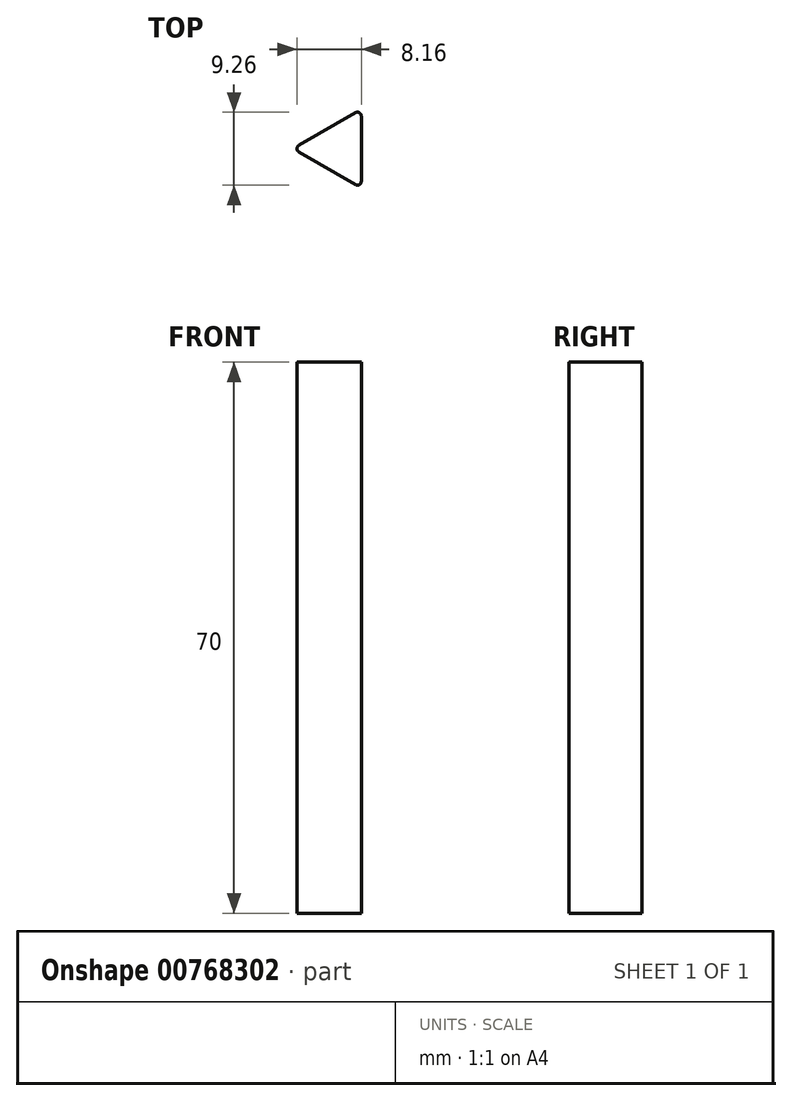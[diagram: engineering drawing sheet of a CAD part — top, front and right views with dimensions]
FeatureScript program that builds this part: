
annotation { "Feature Type Name" : "Feature", "Feature Type Description" : "" }
export const myFeature = defineFeature(function(context is Context, id is Id, definition is map)
    precondition{}
    {
        {
            var Q0;
            Q0=qCreatedBy(makeId("Top.planeOp"),FACE);
            var sketch = newSketch(context, id + "F0", { "sketchPlane" : qUnion([Q0])});
            skCircle(sketch, "E0.cCircle", {"center": v(0, 0) * mm, "radius": 5.77 * mm, "construction": true});
            skLineSegment(sketch, "E0.0", {"start": v(-5.02, 0.43) * mm, "end": v(2.14, 4.57) * mm});
            skLineSegment(sketch, "E0.1", {"start": v(2.89, 4.13) * mm, "end": v(2.89, -4.13) * mm});
            skLineSegment(sketch, "E0.2", {"start": v(2.14, -4.57) * mm, "end": v(-5.02, -0.43) * mm});
            skPoint(sketch, "E1.visualSharp", {"position": v(2.89, 5) * mm});
            skArc(sketch, "E1.filletArc", {"start": v(2.89, 4.13) * mm, "mid": v(2.64, 4.57) * mm, "end": v(2.14, 4.57) * mm});
            skPoint(sketch, "E2.visualSharp", {"position": v(-5.77, 0) * mm});
            skArc(sketch, "E2.filletArc", {"start": v(-5.02, 0.43) * mm, "mid": v(-5.27, 0) * mm, "end": v(-5.02, -0.43) * mm});
            skPoint(sketch, "E3.visualSharp", {"position": v(2.89, -5) * mm});
            skArc(sketch, "E3.filletArc", {"start": v(2.14, -4.57) * mm, "mid": v(2.64, -4.57) * mm, "end": v(2.89, -4.13) * mm});
            skSolve(sketch);
        }
        {
            var Q0;
            Q0=makeQuery(id+"F0.imprint","IMPRINT",FACE,{"disambiguationData":[TD([[makeQuery(id+"F0.imprint","IMPRINT",EDGE,{"derivedFrom":sQuery(id+"F0.wireOp",EDGE,"E0.0")}),-1.0]])]});
            extrude(context, id + "F1", {"entities" : qUnion([Q0]), "depth" : 70 * mm, "offsetDistance" : 25 * mm});
        }
    });
